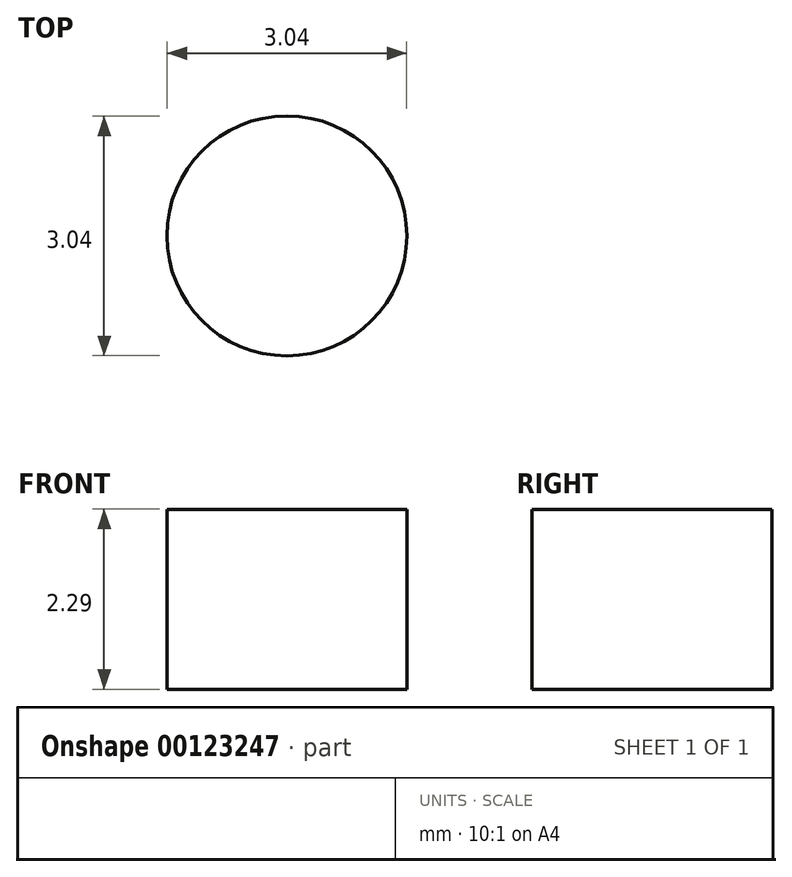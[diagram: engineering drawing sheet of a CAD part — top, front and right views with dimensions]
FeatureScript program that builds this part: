
annotation { "Feature Type Name" : "Feature", "Feature Type Description" : "" }
export const myFeature = defineFeature(function(context is Context, id is Id, definition is map)
    precondition{}
    {
        {
            var Q0;
            Q0=qCreatedBy(makeId("Top.planeOp"),FACE);
            var sketch = newSketch(context, id + "F0", { "sketchPlane" : qUnion([Q0])});
            skCircle(sketch, "E0", {"center": v(0, 0) * mm, "radius": 1.52 * mm});
            skSolve(sketch);
        }
        {
            var Q0;
            Q0 = qSketchRegion(id + "F0", true);
            extrude(context, id + "F1", {"entities" : qUnion([Q0]), "depth" : 2.3 * mm});
        }
    });
